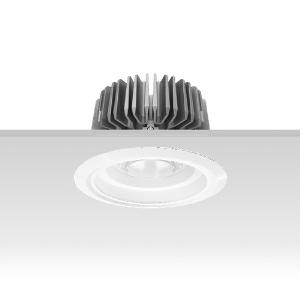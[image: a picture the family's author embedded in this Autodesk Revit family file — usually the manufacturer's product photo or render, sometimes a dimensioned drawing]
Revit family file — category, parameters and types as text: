
# Revit family: 3f_filippi_-_3f_reno_bianco_ampio_3f_filippi_-_30349_a01023_-_3f_reno_150_wh_3000-840_wide___vt_wh_b17a
name_source: partatom
category: Lighting Fixtures
units: mm (PartAtom-declared; Revit-internal decimal feet)

## family parameters
Cut with Voids When Loaded = No
Host = Face
Light Source = No
Part Type = Normal
Room Calculation Point = No
Round Connector Dimension = Use Diameter
Shared = No

## types (1)
- 3F Filippi - 3F Reno Bianco Ampio (1 x LED, 2647 lm, 28 W, 4000 K)
    Apparent Load = 28 VA
    Approval mark = CE
    CIE Flux Codes = 74 93 99 100 100
    Color Rendering = 80
    Color Temperature = 4000 K
    Control Gear = Electronic ballast
    Default Elevation = 1800 mm
    Description = ILLUMINOTECHNICAL
Luminous efficiency 100% (DLOR 100%, ULOR 0%).
Initial luminous flux of the luminaire 2647 lm.
Direct symmetric wide distribution.
Installation Interdistance Transv.D = 1.54 x hu - Long.D = 1.54 x hu.
Tabular UGR (CIE 117 - 4H-8H; S=0.25H; 70/50/20): RUG 24.4 - 24.2.
Beam angle: 74° - 73°.
Luminous efficacy 95 lm/W.
Lifetime (L90/B10): 30000 h. (tq+25°C)
Lifetime (L85/B10): 50000 h. (tq+25°C)
Lifetime (L70/B10): 80000 h. (tq+25°C)
Sudden decreased luminous flux after 50000 hours: 0% (C0).
Photobiological safety in compliance with IEC/TR 62778: RG0 risk exempt, (IEC 62471).
In compliance with IEC/EN 62722-2-1 - IEC/EN 62717 standards.

SOURCE
Compact LED module 3000/840.
Energy efficiency class (UE 2019/2020 - UE 2019/2015): D.
CIE 13.3 Colour rendering index: CRI >80 (R9 <50%).
IES TM-30 Fidelity Index: Rf = 84 Rg = 95.
CCT nominal colour temperature 4000 K.
Colour initial tolerance (MacAdam): SDCM 3.
Zhaga Book 3 compliant.

MECHANICAL
Passive heat dissipator in die-casting aluminium, oversized, for optimum thermal management of the LED module.
Parabolic element with graduated/concentric rings in white polycarbonate.
Transparent external lens with glossy and satin differentiated surfaces, with a cooling and anti-insect system in methacrylate (PMMA).
Fastening spring clips in stainless steel.
Dimensions: diameter 176 mm, height 111 mm. Weight 1.45 kg.
IP44 protection degree for exposed part, IP20 for recessed part.
Mechanical strength to impacts IK06 (1 joule).
Glow-wire test resistance 650°C.

ELECTRICAL
Wiring on a separate unit.
Halogen Free electronic wiring 230V-50/60Hz, power factor 0.95, THD <25%, constant output current, SELV, class II, 1 driver.
Power of the luminaire 28 W.
ENEC - CE.
SAFE FLICKER: PstLM=<1 and SVM=<0.4 (IEC TR 61547-1 and IEC TR 63158), to ensure a more comfortable and safe light.
Luminaire compliant with EN 60598-2-22 for power supply from a centralised emergency system CPSS (Central Power Supply System), not incorporated in the luminaire - high risk areas excluded. The default power and flux are 100% in AC and 100% in DC.
Ambient temperature from 0°C to +25°C.
Temperature class T6 max 85°C.
Relative humidity UR: <85%.

INSTALLATION
Pull-up recessed fitting.
False ceiling carving: 150 mm.
All accessories dedicated to this product are available on the Catalog and on our website www.3F-Filippi.com.

ACCESSORIES
A01023 - VT transparent glass, tempered, not flammable, locked and in line with the trim, in white polycarbonate.

APPLICATIONS
Environments: architectural, commercial, exhibition areas, transit areas, corridors, shops, display windows, service areas.
In false ceilings with narrow voids.

WARNING
Luminaire designed for disposal/recycling at end-of-life.
Replaceable (LED only) light source by a professional. Replaceable control gear by a professional.
    Height = 0 mm  [stored 0 ft]
    Lamp = 1 x LED
    Lamp Light Flux = 2647 lm
    Lamp Power = 28 W
    Lamp count = 1
    Length = 176 mm
    Lifetime = 50000 h
    Luminous efficacy = 95 lm/W
    Manufacturer = 3F Filippi
    ModVariant = No
    Model = 3F Filippi - 30349+A01023 - 3F Reno 150 WH 3000-840 WIDE + VT WH
    Mounting Place = Ceiling
    Mounting Type = Recessed
    Number of Poles = 1
    OnlyDefault = Yes
    Power Factor = 1
    Product Name = 3F Filippi - 3F Reno Bianco Ampio
    Product group = recessed luminaire
    ProductGroupID = 4
    Protection Class = Protection class II
    Protection Degree = IP 20
    RLX_Detail_Level = 1
    RLX_Emergency_Light_Flux = 0 lm
    RLX_Emergency_Type = 0
    RLX_Emergency_Type_DB = No
    RlxData = <blob elided: 85841 chars, md5=16bfa4c8>
    Socket = socket
    Standby Power = 0 W
    System Light Flux = 2647 lm
    System Power = 28 W
    Type Comments = Product without accessories
    Type Image = 3ffilippi_3f_reno_150_wh_d150__a01023.jpg
    URL = http://relux.com
    VarID = ---
    Voltage = 0 V
    Weight = 0.00 kg
    Width = 0 mm  [stored 0 ft]

note: [stored X ft] marks values corroborated as IEEE doubles in the binary element streams (Revit-internal decimal feet)

## geometry (parser evidence)
native form markers: Blend x4, Sweep x11
no freeform markers — native parametric forms only
